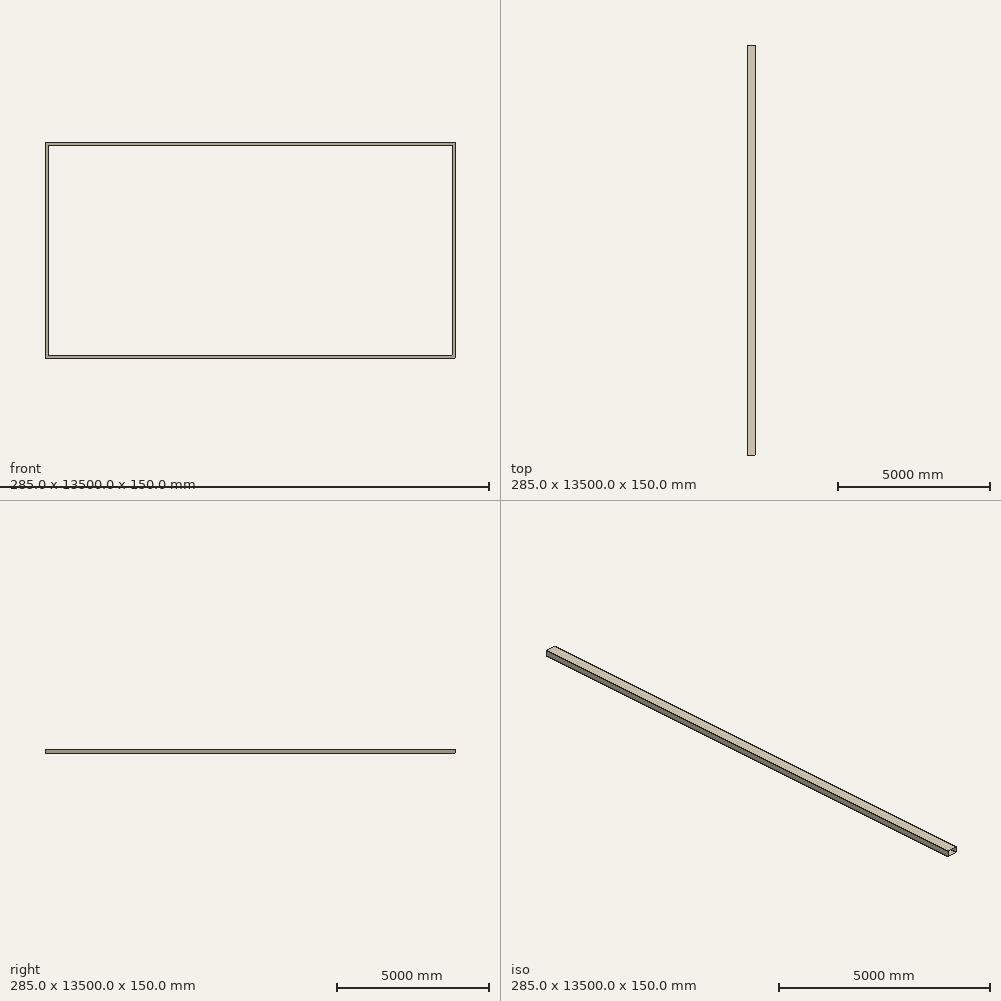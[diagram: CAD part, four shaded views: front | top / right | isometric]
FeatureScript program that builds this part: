
annotation { "Feature Type Name" : "Feature", "Feature Type Description" : "" }
export const myFeature = defineFeature(function(context is Context, id is Id, definition is map)
    precondition{}
    {
        {
            var Q0;
            Q0=qCreatedBy(makeId("Front.planeOp"),FACE);
            var sketch = newSketch(context, id + "F0", { "sketchPlane" : qUnion([Q0])});
            skLineSegment(sketch, "E0.bottom", {"start": v(0, 0) * mm, "end": v(285, 0) * mm});
            skLineSegment(sketch, "E0.top", {"start": v(0, 150) * mm, "end": v(285, 150) * mm});
            skLineSegment(sketch, "E0.left", {"start": v(0, 0) * mm, "end": v(0, 150) * mm});
            skLineSegment(sketch, "E0.right", {"start": v(285, 0) * mm, "end": v(285, 150) * mm});
            skLineSegment(sketch, "E1.bottom", {"start": v(2, 2) * mm, "end": v(283, 2) * mm});
            skLineSegment(sketch, "E1.top", {"start": v(2, 148) * mm, "end": v(283, 148) * mm});
            skLineSegment(sketch, "E1.left", {"start": v(2, 2) * mm, "end": v(2, 148) * mm});
            skLineSegment(sketch, "E1.right", {"start": v(283, 2) * mm, "end": v(283, 148) * mm});
            skSolve(sketch);
        }
        {
            var Q0;
            Q0 = qSketchRegion(id + "F0", true);
            extrude(context, id + "F1", {"entities" : qUnion([Q0]), "depth" : 13500 * mm, "offsetDistance" : 25 * mm});
        }
    });
